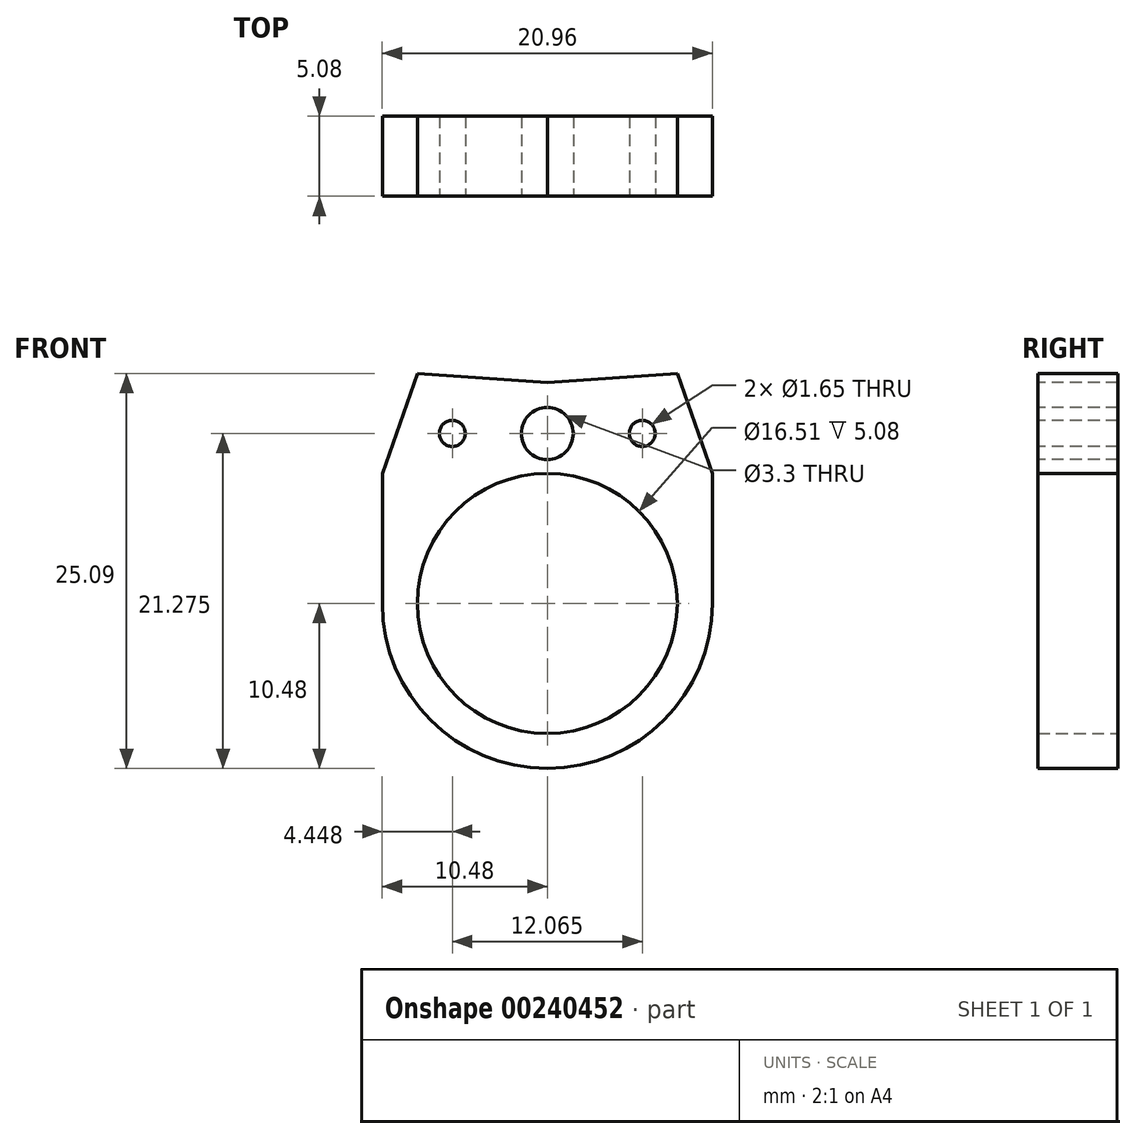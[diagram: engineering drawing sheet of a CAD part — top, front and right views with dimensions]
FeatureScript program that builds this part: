
annotation { "Feature Type Name" : "Feature", "Feature Type Description" : "" }
export const myFeature = defineFeature(function(context is Context, id is Id, definition is map)
    precondition{}
    {
        {
            var Q0;
            Q0=qCreatedBy(makeId("Front.planeOp"),FACE);
            var sketch = newSketch(context, id + "F0", { "sketchPlane" : qUnion([Q0])});
            skCircle(sketch, "E0", {"center": v(0, 0) * mm, "radius": 8.26 * mm});
            skCircle(sketch, "E1", {"center": v(0, 0) * mm, "radius": 10.48 * mm});
            skLineSegment(sketch, "E2", {"start": v(-10.48, 0) * mm, "end": v(-10.48, 8.25) * mm});
            skLineSegment(sketch, "E3", {"start": v(10.48, 0) * mm, "end": v(10.48, 8.25) * mm});
            skLineSegment(sketch, "E4", {"start": v(-10.48, 8.25) * mm, "end": v(-6.03, 10.8) * mm});
            skLineSegment(sketch, "E5", {"start": v(-6.03, 10.8) * mm, "end": v(6.03, 10.8) * mm});
            skLineSegment(sketch, "E6", {"start": v(6.03, 10.8) * mm, "end": v(10.48, 8.25) * mm});
            skSolve(sketch);
        }
        {
            var Q0;
            {var subQ1=sQuery(id+"F0.wireOp",EDGE,"E2");Q0=makeQuery(id+"F0.imprint","IMPRINT",FACE,{"disambiguationData":[TD([[makeQuery(id+"F0.imprint","IMPRINT",EDGE,{"derivedFrom":subQ1}),-1.0]])]});}
            var Q1;
            Q1=makeQuery(id+"F0.imprint","IMPRINT",FACE,{"disambiguationData":[TD([[makeQuery(id+"F0.imprint","IMPRINT",EDGE,{"derivedFrom":sQuery(id+"F0.wireOp",EDGE,"E0")}),-1.0]])]});
            extrude(context, id + "F1", {"entities" : qUnion([Q0, Q1]), "depth" : 5.08 * mm});
        }
        {
            var Q0;
            Q0=makeQuery(id+"F1.opExtrude","CAP_FACE",FACE,{"disambiguationData":[OSD([sQuery(id+"F0.wireOp",EDGE,"E0"),sQuery(id+"F0.wireOp",EDGE,"E1"),sQuery(id+"F0.wireOp",EDGE,"E2"),sQuery(id+"F0.wireOp",EDGE,"E3"),sQuery(id+"F0.wireOp",EDGE,"E4"),sQuery(id+"F0.wireOp",EDGE,"E5"),sQuery(id+"F0.wireOp",EDGE,"E6")])],"isStart":false});
            var sketch = newSketch(context, id + "F2", { "sketchPlane" : qUnion([Q0])});
            skLineSegment(sketch, "E7", {"start": v(-8.26, 14.6) * mm, "end": v(0, 14.03) * mm});
            skLineSegment(sketch, "E8", {"start": v(8.26, 14.6) * mm, "end": v(0, 14.03) * mm});
            skLineSegment(sketch, "E9", {"start": v(-8.26, 14.6) * mm, "end": v(-10.48, 8.25) * mm});
            skLineSegment(sketch, "E10", {"start": v(8.26, 14.6) * mm, "end": v(10.48, 8.25) * mm});
            skLineSegment(sketch, "E11", {"start": v(-10.48, 8.25) * mm, "end": v(-6.03, 10.8) * mm});
            skLineSegment(sketch, "E12", {"start": v(-6.03, 10.8) * mm, "end": v(6.03, 10.8) * mm});
            skLineSegment(sketch, "E13", {"start": v(6.03, 10.8) * mm, "end": v(10.48, 8.25) * mm});
            skSolve(sketch);
        }
        {
            var Q0;
            Q0=makeQuery(id+"F2.imprint","IMPRINT",FACE,{"disambiguationData":[TD([[makeQuery(id+"F2.imprint","IMPRINT",EDGE,{"derivedFrom":sQuery(id+"F2.wireOp",EDGE,"E7")}),-1.0]])]});
            extrude(context, id + "F3", {"entities" : qUnion([Q0]), "operationType" : NewBodyOperationType.ADD, "oppositeDirection" : true, "depth" : 5.08 * mm});
        }
        {
            var Q0;
            Q0=makeQuery(id+"F2.imprint","IMPRINT",FACE,{"disambiguationData":[TD([[makeQuery(id+"F2.imprint","IMPRINT",EDGE,{"derivedFrom":sQuery(id+"F2.wireOp",EDGE,"E11")}),-1.0]])]});
            var sketch = newSketch(context, id + "F4", { "sketchPlane" : qUnion([Q0])});
            skCircle(sketch, "E14", {"center": v(0, 10.8) * mm, "radius": 1.65 * mm});
            skCircle(sketch, "E15", {"center": v(6.03, 10.8) * mm, "radius": 0.83 * mm});
            skCircle(sketch, "E16", {"center": v(-6.03, 10.8) * mm, "radius": 0.83 * mm});
            skSolve(sketch);
        }
        {
            var Q0;
            Q0 = qSketchRegion(id + "F4", true);
            extrude(context, id + "F5", {"entities" : qUnion([Q0]), "operationType" : NewBodyOperationType.REMOVE, "oppositeDirection" : true, "depth" : 25.4 * mm});
        }
    });
